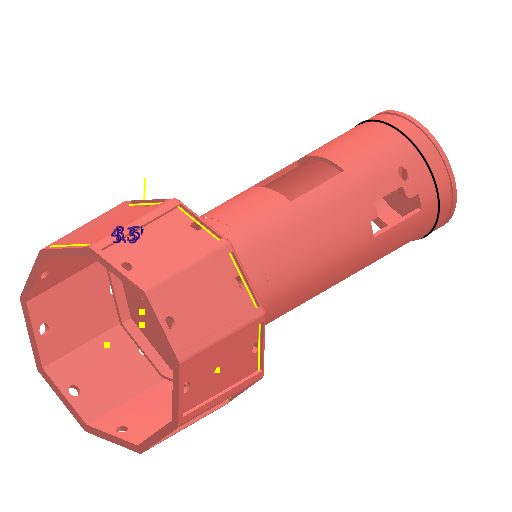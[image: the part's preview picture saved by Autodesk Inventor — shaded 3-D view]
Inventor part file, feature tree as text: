
AUTODESK INVENTOR PART (.ipt)
format: ipt  version: 2025 (Build 290162000, 162)  size: 1,875,456 bytes
history: native  units: in
note: dims shown in document units (in); Inventor stores cm internally (conversion verified against a paired STEP export)
features: sketch x63, extrude x58, fillet x9, plane x6, other x3, direct_edit x2, pattern_circular x2, move_body x2, reference x2, emboss x1, split x1, projected_geometry x1
ambient origin geometry x8: Origin, YZ Plane, XZ Plane, XY Plane, X Axis, Y Axis, Z Axis, Center Point
bodies: Solid1 (feature_tree), Body4 (feature_tree), Solid2 (feature_tree), Solid3 (feature_tree)
feature tree (150):
  direct_edit  "Direct Edit1"
  extrude  "Extrusion1"  Depth=0.2062in TaperAngle=0.0deg
  extrude  "Extrusion2"  Depth=0.1437in TaperAngle=0.0deg
  sketch  "Sketch3"  dims[d8=0.0787in d9=1.811in d10=0.0in]
  extrude  "Extrusion3"  Depth=1.811in TaperAngle=0.0deg
  sketch  "Sketch6"  dims[d13=0.0591in d14=0.0in d15=0.1969in]
  extrude  "Extrusion4"  Depth=0.9449in
  extrude  "Extrusion5"  Depth=0.1969in
  pattern_circular  "Circular Pattern1"  Count=9  [1 undecoded]
  extrude  "Extrusion6"  Depth=0.315in
  extrude  "Extrusion7"  Depth=1.4409in TaperAngle=0.0deg
  pattern_circular  "Circular Pattern2"  Count=9  [1 undecoded]
  fillet  "Fillet1"  Radius=0.1412in
  extrude  "Extrusion8"  Depth=0.063in
  extrude  "Extrusion9"  Depth=0.8312in TaperAngle=0.0deg
  extrude  "Extrusion10"  Depth=0.0787in
  extrude  "Extrusion11"  Depth=0.1688in TaperAngle=0.0deg
  direct_edit  "Direct Edit2"
  extrude  "Extrusion12"  Depth=1.1063in TaperAngle=0.0deg
  extrude  "Extrusion13"  Depth=0.4724in TaperAngle=0.0deg
  extrude  "Extrusion14"  Depth=1.8898in
  extrude  "Extrusion15"  Depth=1.2795in
  extrude  "Extrusion16"  Depth=0.0787in TaperAngle=0.0deg
  extrude  "Extrusion17"  Depth=0.0787in
  fillet  "Fillet2"  Radius=0.0787in
  fillet  "Fillet3"  Radius=0.0787in
  fillet  "Fillet4"  Radius=0.7338in
  fillet  "Fillet5"  Radius=0.3937in
  extrude  "Extrusion18"  Depth=0.8312in TaperAngle=0.0deg
  extrude  "Extrusion19"  Depth=0.1575in TaperAngle=0.0deg
  extrude  "Extrusion20"  Depth=0.1969in TaperAngle=0.0deg
  fillet  "Fillet6"  Radius=0.1781in
  sketch  "Sketch24"  dims[d78=1.3912in d79=0.1969in d80=0.0in d81=0.1781in d82=0.0in]
  extrude  "Extrusion22"  Depth=1.5438in TaperAngle=0.0deg
  fillet  "Fillet8"  Radius=2.7938in
  extrude  "Extrusion23"  Depth=0.2362in
  extrude  "Extrusion24"  Depth=1.7313in TaperAngle=0.0deg
  extrude  "Extrusion25"  Depth=0.1575in
  sketch  "Sketch30"  dims[d98=0.1575in d99=1.6334in d100=0.0in]
  sketch  "Sketch32"  dims[d101=3.5084in d102=0.0in d103=0.9459in d104=0.6917in d105=0.0in d106=0.0in]
  extrude  "Extrusion26"  Depth=1.6334in TaperAngle=0.0deg
  extrude  "Extrusion27"  Depth=0.9459in TaperAngle=0.0deg
  plane  "Work Plane3"
  extrude  "Extrusion28"  Depth=0.0787in TaperAngle=0.0deg
  sketch  "Sketch37"  dims[d118=0.0in d119=0.0in d120=0.0in d121=-0.3937in]
  extrude  "Extrusion29"  Depth=0.9375in
  extrude  "Extrusion30"  Depth=1.3563in TaperAngle=0.0deg
  extrude  "Extrusion31"  TaperAngle=0.0deg  [1 undecoded]
  extrude  "Extrusion32"  Depth=1.4562in TaperAngle=0.0deg
  sketch  "Sketch42"  dims[d136=4.9173in d137=0.0in d138=2.6535in d139=0.0in]
  extrude  "Extrusion33"  Depth=4.4562in TaperAngle=0.0deg
  sketch  "Sketch44"  dims[d144=0.6063in d145=0.0in d146=0.1378in]
  sketch  "Sketch45"  dims[d147=3.4188in d148=0.0in d149=0.2687in d150=0.0in]
  extrude  "Extrusion34"  Depth=0.9173in TaperAngle=0.0deg
  extrude  "Extrusion35"  Depth=2.6535in TaperAngle=0.0deg
  plane  "Work Plane6"
  plane  "Work Plane7"
  extrude  "Extrusion36"  Depth=4.4562in TaperAngle=0.0deg
  sketch  "Sketch49"  dims[d163=0.2062in d164=0.0in d165=0.2062in d166=0.0in]
  plane  "Work Plane8"
  emboss  "Emboss1"
  extrude  "Extrusion37"  Depth=0.1378in
  plane  "Work Plane9"
  split  "Split1"
  move_body  "Move Body1"
  extrude  "Extrusion38"  Depth=0.2687in TaperAngle=0.0deg
  extrude  "Extrusion39"  Depth=3.5438in TaperAngle=0.0deg
  sketch  "Sketch54"
  extrude  "Extrusion40"  Depth=0.0812in TaperAngle=0.0deg
  extrude  "Extrusion41"  Depth=0.2953in TaperAngle=0.0deg
  extrude  "Extrusion42"  Depth=0.2062in TaperAngle=0.0deg
  extrude  "Extrusion43"  Depth=0.0787in
  extrude  "Extrusion44"  Depth=0.1388in TaperAngle=0.0deg
  extrude  "Extrusion45"  Depth=0.1388in TaperAngle=0.0deg
  extrude  "Extrusion46"  [1 undecoded]
  extrude  "Extrusion47"  [1 undecoded]
  sketch  "Sketch56"
  extrude  "Extrusion48"  [1 undecoded]
  extrude  "Extrusion49"  [1 undecoded]
  extrude  "Extrusion50"  [1 undecoded]
  extrude  "Extrusion51"  [1 undecoded]
  extrude  "Extrusion52"  [1 undecoded]
  extrude  "Extrusion53"  [1 undecoded]
  extrude  "Extrusion54"  [1 undecoded]
  extrude  "Extrusion55"  [1 undecoded]
  extrude  "Extrusion56"  [1 undecoded]
  fillet  "Fillet13"  [1 undecoded]
  fillet  "Fillet14"  [1 undecoded]
  extrude  "Extrusion57"  [1 undecoded]
  extrude  "Extrusion58"  [1 undecoded]
  sketch  "Sketch67"
  sketch  "Sketch68"
  extrude  "Extrusion59"  [1 undecoded]
  sketch  "Sketch1"  dims[d0=0.0in d1=0.0in d2=-0.6875in d3=0.2062in d4=0.0in]
  sketch  "Sketch2"  dims[d5=1.1811in d6=0.1437in d7=0.0in]
  sketch  "Sketch5"  dims[d11=1.7323in d12=0.9449in]
  sketch  "Sketch7"  dims[d16=0.1969in]
  sketch  "Sketch8"  dims[d17=0.1841in d18=0.0in d19=3.5433in d20=2.4737in]
  sketch  "Sketch9"  dims[d22=0.0787in d23=0.315in]
  sketch  "Sketch10"  dims[d24=0.0787in d25=1.4409in d26=0.0in]
  sketch  "Sketch11"  dims[d27=1.9966in d28=0.0in d29=3.5433in d30=2.4737in d32=0.1412in]
  sketch  "Sketch12"  dims[d33=0.063in d34=0.063in]
  sketch  "Sketch13"  dims[d35=0.2756in d36=0.0in d37=0.8312in d38=0.0in]
  sketch  "Sketch14"  dims[d39=1.1063in d40=0.0in d41=0.0787in]
  sketch  "Sketch15"  dims[d42=0.0787in d43=0.1688in d44=0.0in]
  sketch  "Sketch16"  dims[d45=0.5187in d46=0.0in d47=1.1063in d48=0.0in]
  sketch  "Sketch17"  dims[d49=1.6535in d50=0.4724in d51=0.0in]
  sketch  "Sketch18"  dims[d52=0.0787in d53=0.0in d54=1.8898in]
  sketch  "Sketch19"  dims[d55=0.2963in d56=0.0in d57=1.2795in]
  sketch  "Sketch20"  dims[d58=1.3583in d59=0.0787in d60=0.0in]
  sketch  "Sketch21"  dims[d61=0.0787in d62=0.0787in d63=0.0787in d64=0.0787in d65=0.7338in d66=0.0in d67=0.3937in d68=0.0in]
  sketch  "Sketch22"  dims[d69=0.0787in d70=0.8312in d71=0.0in]
  sketch  "Sketch23"  dims[d72=0.0787in d76=0.1575in d77=0.0in]
  sketch  "Sketch26"  dims[d83=0.1575in d84=0.0in d85=1.5438in d86=0.0in d87=2.7938in d88=0.0in]
  sketch  "Sketch27"  dims[d89=1.7313in d90=0.0in d91=0.2362in]
  sketch  "Sketch28"  dims[d92=0.2362in d93=1.7313in d94=0.0in]
  sketch  "Sketch29"  dims[d95=0.0709in d96=0.0in d97=0.1575in]
  sketch  "Sketch33"  dims[d107=0.1137in d108=0.0in d109=0.0787in d110=0.0in]
  sketch  "Sketch34"  dims[d111=1.6688in d112=0.0in d113=0.9375in]
  sketch  "Sketch36"  dims[d114=0.0394in d115=0.0in d116=1.3563in d117=0.0in]
  reference  "Reference1"
  reference  "Reference2"
  sketch  "Sketch39"  dims[d122=0.3937in d123=0.0in d124=1.4562in d125=0.0in]
  sketch  "Sketch40"  dims[d130=0.1693in d131=4.4562in d132=0.0in]
  sketch  "Sketch41"  dims[d133=0.2165in d134=0.9173in d135=0.0in]
  sketch  "Sketch43"  dims[d140=0.9247in d141=0.0in d142=4.4562in d143=0.0in]
  sketch  "Sketch46"  dims[d151=0.4813in d152=0.0in d153=3.5438in d154=0.0in]
  sketch  "Sketch47"  dims[d155=0.3937in d156=0.0in d157=0.0812in d158=0.0in]
  plane  "Work Plane5"
  sketch  "Sketch48"  dims[d159=0.2953in d160=0.0in d161=0.2953in d162=0.0in]
  sketch  "Sketch50"  dims[d167=0.0787in d168=0.0787in]
  sketch  "Sketch51"  dims[d169=1.7313in d170=0.0in d171=0.1388in d172=0.0in]
  sketch  "Sketch52"  dims[d173=1.9291in d174=0.1388in d175=0.0in]
  sketch  "Sketch53"
  sketch  "Sketch55"
  sketch  "Sketch57"
  sketch  "Sketch58"
  sketch  "Sketch59"
  sketch  "Sketch60"
  sketch  "Sketch61"
  sketch  "Sketch62"
  sketch  "Sketch63"
  sketch  "Sketch64"
  sketch  "Sketch65"
  sketch  "Sketch66"
  move_body  "Move1"
  projected_geometry  "Project Cut Edges1"
  other  "Delete1"
  other  "Full assembly 2.iam"
  other  "main_board:1"
note: 19 required parameter values undecoded (feature->parameter linkage not recoverable at this tier; creation-order binding heuristic only, values carry confidence <= 0.55)
